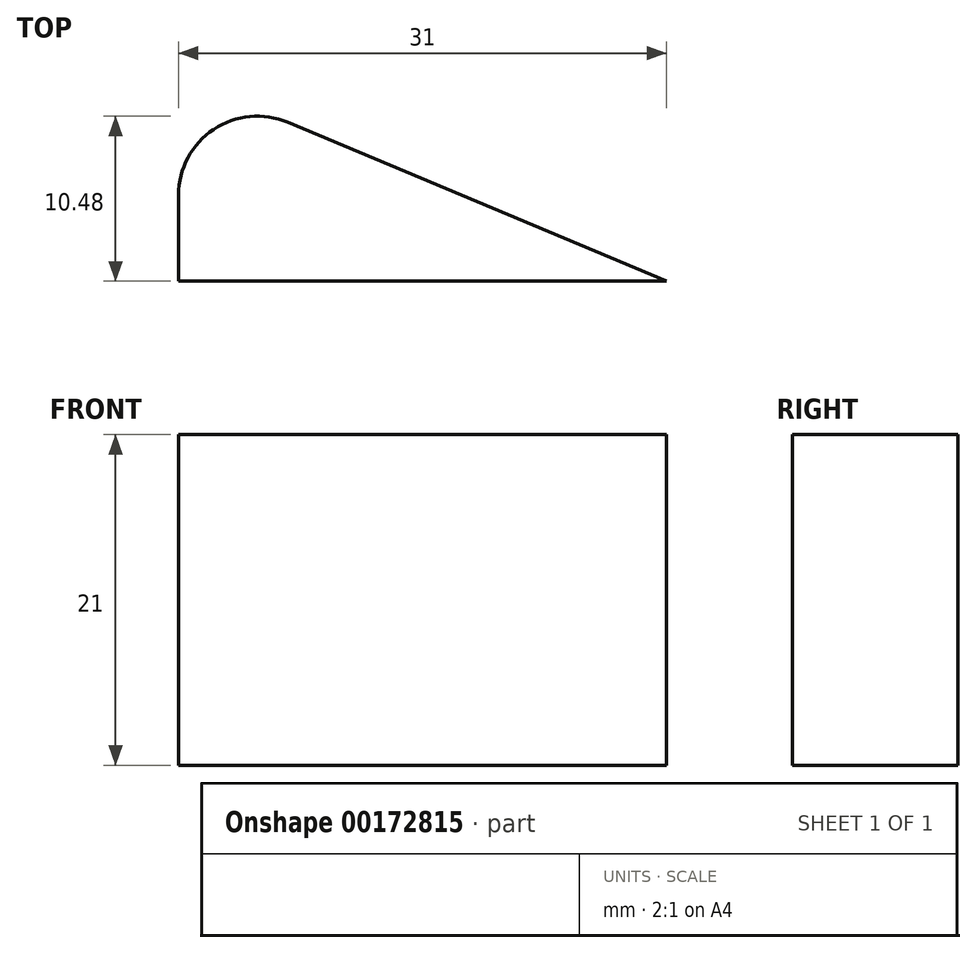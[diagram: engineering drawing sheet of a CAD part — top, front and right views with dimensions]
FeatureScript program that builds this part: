
annotation { "Feature Type Name" : "Feature", "Feature Type Description" : "" }
export const myFeature = defineFeature(function(context is Context, id is Id, definition is map)
    precondition{}
    {
        {
            var Q0;
            Q0=qCreatedBy(makeId("Top.planeOp"),FACE);
            var sketch = newSketch(context, id + "F0", { "sketchPlane" : qUnion([Q0])});
            skLineSegment(sketch, "E0", {"start": v(0, 0) * mm, "end": v(31, 0) * mm});
            skLineSegment(sketch, "E1", {"start": v(0, 0) * mm, "end": v(0, 13) * mm});
            skLineSegment(sketch, "E2", {"start": v(0, 13) * mm, "end": v(31, 0) * mm});
            skSolve(sketch);
        }
        {
            var Q0;
            Q0=makeQuery(id+"F0.imprint","IMPRINT",FACE,{"disambiguationData":[TD([[makeQuery(id+"F0.imprint","IMPRINT",EDGE,{"derivedFrom":sQuery(id+"F0.wireOp",EDGE,"E1")}),1.0]])]});
            var Q1;
            Q1=makeQuery(id+"F0.imprint","IMPRINT",FACE,{"disambiguationData":[TD([[makeQuery(id+"F0.imprint","IMPRINT",EDGE,{"derivedFrom":sQuery(id+"F0.wireOp",EDGE,"E0")}),1.0]])]});
            extrude(context, id + "F1", {"entities" : qUnion([Q0, Q1]), "depth" : 21 * mm});
        }
        {
            var Q0;
            Q0=makeQuery(id+"F1.opExtrude","SWEPT_EDGE",EDGE,{"disambiguationData":[OSD([sQuery(id+"F0.wireOp",EDGE,"E1"),sQuery(id+"F0.wireOp",EDGE,"E2")])]});
            fillet(context, id + "F2", {"entities" : qUnion([Q0]), "radius" : 5 * mm, "tangentPropagation" : true, "allowEdgeOverflow" : false});
        }
    });
